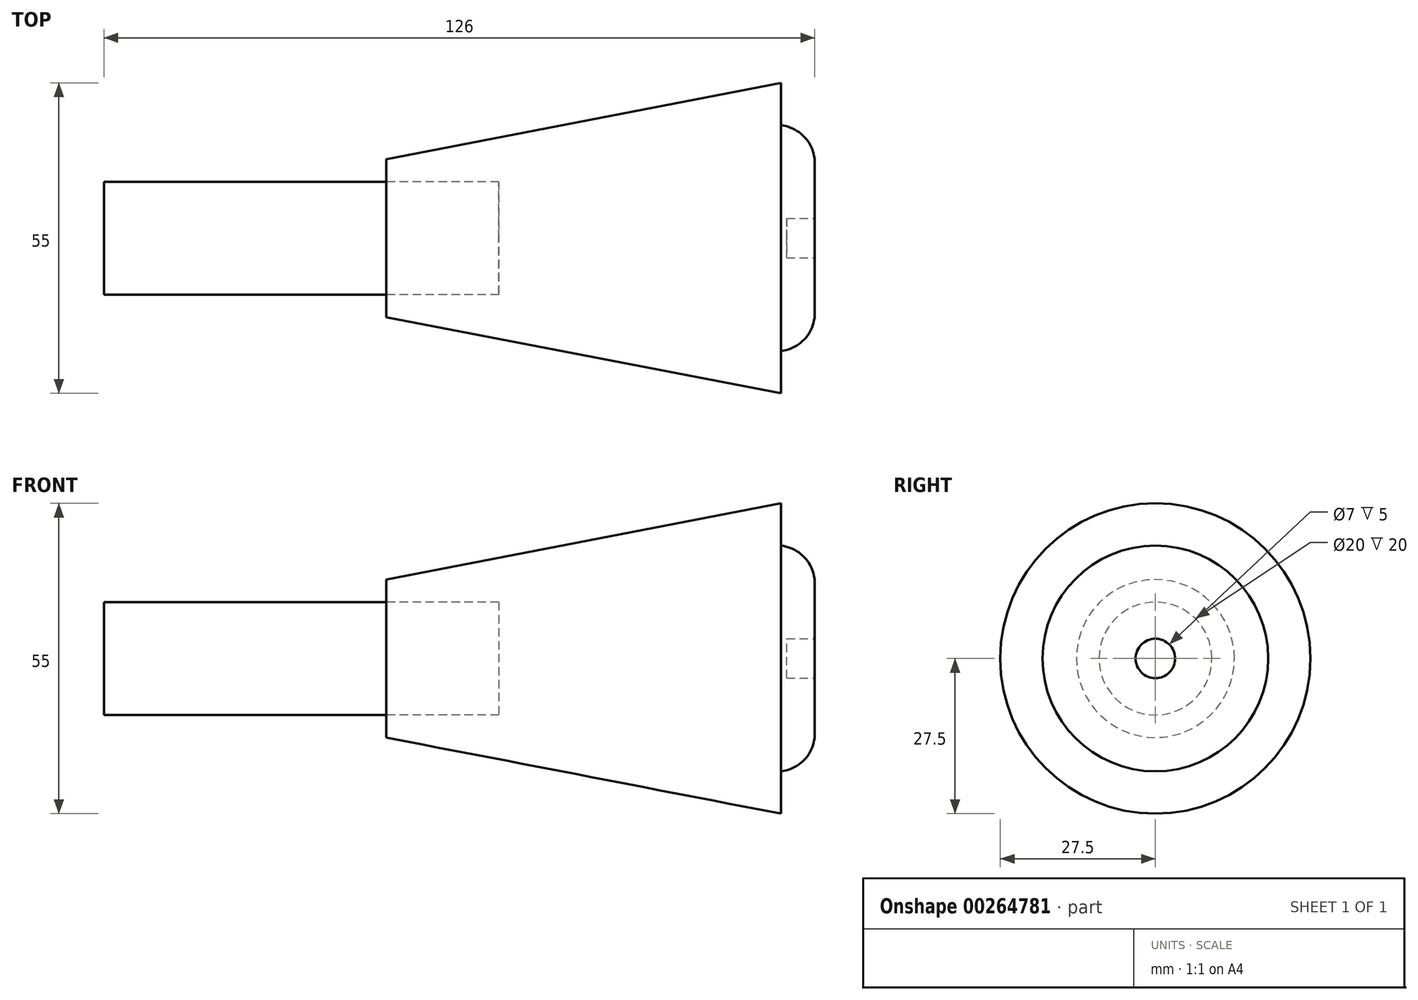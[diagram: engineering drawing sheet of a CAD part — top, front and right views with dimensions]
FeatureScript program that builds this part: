
annotation { "Feature Type Name" : "Feature", "Feature Type Description" : "" }
export const myFeature = defineFeature(function(context is Context, id is Id, definition is map)
    precondition{}
    {
        {
            var Q0;
            Q0=qCreatedBy(makeId("Right.planeOp"),FACE);
            cPlane(context, id + "F0", {"entities" : qUnion([Q0]), "cplaneType" : CPlaneType.OFFSET, "offset" : 70 * mm, "width" : 150 * mm, "height" : 150 * mm});
        }
        {
            var Q0;
            Q0=qCreatedBy(id+"F0.planeOp",FACE);
            var sketch = newSketch(context, id + "F1", { "sketchPlane" : qUnion([Q0])});
            skCircle(sketch, "E0", {"center": v(0, 0) * mm, "radius": 27.5 * mm});
            skLineSegment(sketch, "E1", {"start": v(0, 27.5) * mm, "end": v(0, -27.5) * mm, "construction": true});
            skLineSegment(sketch, "E2", {"start": v(0, 20) * mm, "end": v(0, -20) * mm, "construction": true});
            skSolve(sketch);
        }
        {
            var Q0;
            Q0=qCreatedBy(makeId("Right.planeOp"),FACE);
            var sketch = newSketch(context, id + "F2", { "sketchPlane" : qUnion([Q0])});
            skCircle(sketch, "E3", {"center": v(0, 0) * mm, "radius": 14 * mm});
            skLineSegment(sketch, "E4", {"start": v(14, 0) * mm, "end": v(-14, 0) * mm, "construction": true});
            skSolve(sketch);
        }
        {
            var Q0;
            Q0=makeQuery(id+"F1.imprint","IMPRINT",FACE,{"disambiguationData":[TD([[makeQuery(id+"F1.imprint","IMPRINT",EDGE,{"derivedFrom":sQuery(id+"F1.wireOp",EDGE,"E0")}),1.0]])]});
            var Q1;
            Q1=makeQuery(id+"F2.imprint","IMPRINT",FACE,{"disambiguationData":[TD([[makeQuery(id+"F2.imprint","IMPRINT",EDGE,{"derivedFrom":sQuery(id+"F2.wireOp",EDGE,"E3")}),1.0]])]});
            loft(context, id + "F3", {"sheetProfilesArray" : [{ "sheetProfileEntities" : qUnion([Q0]) }, { "sheetProfileEntities" : qUnion([Q1]) }]});
        }
        {
            var Q0;
            Q0=makeQuery(id+"F3.opLoft","CAP_FACE",FACE,{"disambiguationData":[OSD([makeQuery(id+"F1.imprint","IMPRINT",FACE,{"disambiguationData":[TD([[makeQuery(id+"F1.imprint","IMPRINT",EDGE,{"derivedFrom":sQuery(id+"F1.wireOp",EDGE,"E0")}),1.0]])]})])],"isStart":true});
            var sketch = newSketch(context, id + "F4", { "sketchPlane" : qUnion([Q0])});
            skCircle(sketch, "E5", {"center": v(0, 0) * mm, "radius": 20 * mm});
            skLineSegment(sketch, "E6", {"start": v(-20, 0) * mm, "end": v(20, 0) * mm, "construction": true});
            skSolve(sketch);
        }
        {
            var Q0;
            Q0=makeQuery(id+"F4.imprint","IMPRINT",FACE,{"disambiguationData":[TD([[makeQuery(id+"F4.imprint","IMPRINT",EDGE,{"derivedFrom":sQuery(id+"F4.wireOp",EDGE,"E5")}),1.0]])]});
            extrude(context, id + "F5", {"entities" : qUnion([Q0]), "operationType" : NewBodyOperationType.ADD, "depth" : 6 * mm, "offsetDistance" : 25 * mm});
        }
        {
            var Q0;
            Q0=makeQuery(id+"F5.opExtrude","CAP_FACE",FACE,{"disambiguationData":[OSD([sQuery(id+"F4.wireOp",EDGE,"E5")])],"isStart":false});
            fillet(context, id + "F6", {"entities" : qUnion([Q0]), "radius" : 6.76 * mm, "tangentPropagation" : true, "allowEdgeOverflow" : false});
        }
        {
            var Q0;
            Q0=makeQuery(id+"F5.opExtrude","CAP_FACE",FACE,{"disambiguationData":[OSD([sQuery(id+"F4.wireOp",EDGE,"E5")])],"isStart":false});
            var sketch = newSketch(context, id + "F7", { "sketchPlane" : qUnion([Q0])});
            skCircle(sketch, "E7", {"center": v(0, 0) * mm, "radius": 3.5 * mm});
            skLineSegment(sketch, "E8", {"start": v(-3.5, 0) * mm, "end": v(3.5, 0) * mm, "construction": true});
            skSolve(sketch);
        }
        {
            var Q0;
            Q0=makeQuery(id+"F7.imprint","IMPRINT",FACE,{"disambiguationData":[TD([[makeQuery(id+"F7.imprint","IMPRINT",EDGE,{"derivedFrom":sQuery(id+"F7.wireOp",EDGE,"E7")}),1.0]])]});
            extrude(context, id + "F8", {"entities" : qUnion([Q0]), "operationType" : NewBodyOperationType.REMOVE, "oppositeDirection" : true, "depth" : 5 * mm, "offsetDistance" : 25 * mm});
        }
        {
            var Q0;
            Q0=makeQuery(id+"F3.opLoft","CAP_FACE",FACE,{"disambiguationData":[OSD([makeQuery(id+"F2.imprint","IMPRINT",FACE,{"disambiguationData":[TD([[makeQuery(id+"F2.imprint","IMPRINT",EDGE,{"derivedFrom":sQuery(id+"F2.wireOp",EDGE,"E3")}),1.0]])]})])],"isStart":true});
            var sketch = newSketch(context, id + "F9", { "sketchPlane" : qUnion([Q0])});
            skCircle(sketch, "E9", {"center": v(0, 0) * mm, "radius": 10 * mm});
            skLineSegment(sketch, "E10", {"start": v(-10, 0) * mm, "end": v(10, 0) * mm, "construction": true});
            skSolve(sketch);
        }
        {
            var Q0;
            Q0=makeQuery(id+"F9.imprint","IMPRINT",FACE,{"disambiguationData":[TD([[makeQuery(id+"F9.imprint","IMPRINT",EDGE,{"derivedFrom":sQuery(id+"F9.wireOp",EDGE,"E9")}),1.0]])]});
            extrude(context, id + "F10", {"entities" : qUnion([Q0]), "depth" : 50 * mm, "offsetDistance" : 25 * mm});
        }
        {
            var Q0;
            Q0 = qSketchRegion(id + "F9", true);
            extrude(context, id + "F11", {"entities" : qUnion([Q0]), "operationType" : NewBodyOperationType.REMOVE, "oppositeDirection" : true, "depth" : 20 * mm, "offsetDistance" : 25 * mm});
        }
    });
